# Revit family: E-315_RFA
name_source: partatom
category: Aparatos sanitarios
units: mm (PartAtom-declared; Revit-internal decimal feet)

## family parameters
Activar corte en vistas = No
Compartido = Sí
Corte con vacíos al cargar = No
Cota de conector redondo = Usar diámetro
Mantener orientación de anotación = No
Número OmniClass = 23.45.55.17
Punto de cálculo de habitación = Sí
Se basa en plano de trabajo = No
Siempre vertical = Sí
Tipo de pieza = Normal
Título OmniClass = Mixing Faucets

## types (1)
- E-310
    Acabados = AI Acero Inoxidable, EB Ébano
    Acero Inoxidable = Steel - Polished
    Características = Monomando electrónico para fregadero de cabeza
retráctil con 3 tipos de chorros.
Cartucho de 35 mm
Discos cerámicos de alta dureza que aseguran y
prolongan la vida útil del cartucho sin fugas.
Aireador oculto para chorro aireado.
Facil instalación y mantenimiento.
    Comentarios de tipo = Monomando para Fregadero Electrónico con Sensor Lateral de Baterías, Cabezal Rectráctil con Nudo Móvil, Tres Tipos de Chorro
    Descripción = Llave de cocina
    Electrónico = Sensor infrarojo: Detección de 1 cm a 7 cm
Tensión de alimentación: 3Vcc
Potencia: 0,2 mW, 2 baterías alcalinas "AAA"
    Elevación por defecto = 35"
    Fabricante = HELVEX S.A. de C.V.
    Garantía = El producto HELVEX está garantizado como
libre de defectos en materiales, mano de obra y
procesos de fabricación.
El producto HELVEX está garantizado,en lo que
se refiere a los acabados, por 10 años para los
acabados Cromo y Duravex, y por 2 años en
acabados diferentes al Cromo y Duravex.
Las piezas que sufren desgaste natural en el
producto están garantizadas para uso
residencial por 5 años, y para uso comercial por
3 años.
Todas las partes electrónicas están
garantizadas por defectos de fabricación y mano
de obra por un periodo de 3 años.
La vigencia de la garantía inicia a partir de la
fecha de entrega del producto al consumidor
indicada en la Póliza de Garantía.
    Gasto = Máximo 8,0 LPM
    Imagen de tipo = <Ninguno>
    Inlet Threads = ½" - 14 NPSM
    Max. Working Pressure = 14.2 psi
    Min. Working Pressure = 85.3 psi
    Modelo = E-315
    Operación = Para activar la salida, jale la palanca y después
acerque la mano al sensor para abrir el flujo del agua.
Vuelva a acercar la mano al sensor para cerrar el flujo
de agua.
Para un cierre total, empuje la palanca.
    Support Base Diameter = 2"
    Total Height = 17"
    Total Length = 11"
    Total Width = 4"

## geometry (parser evidence)
native form markers: Sweep x3
no freeform markers — native parametric forms only
